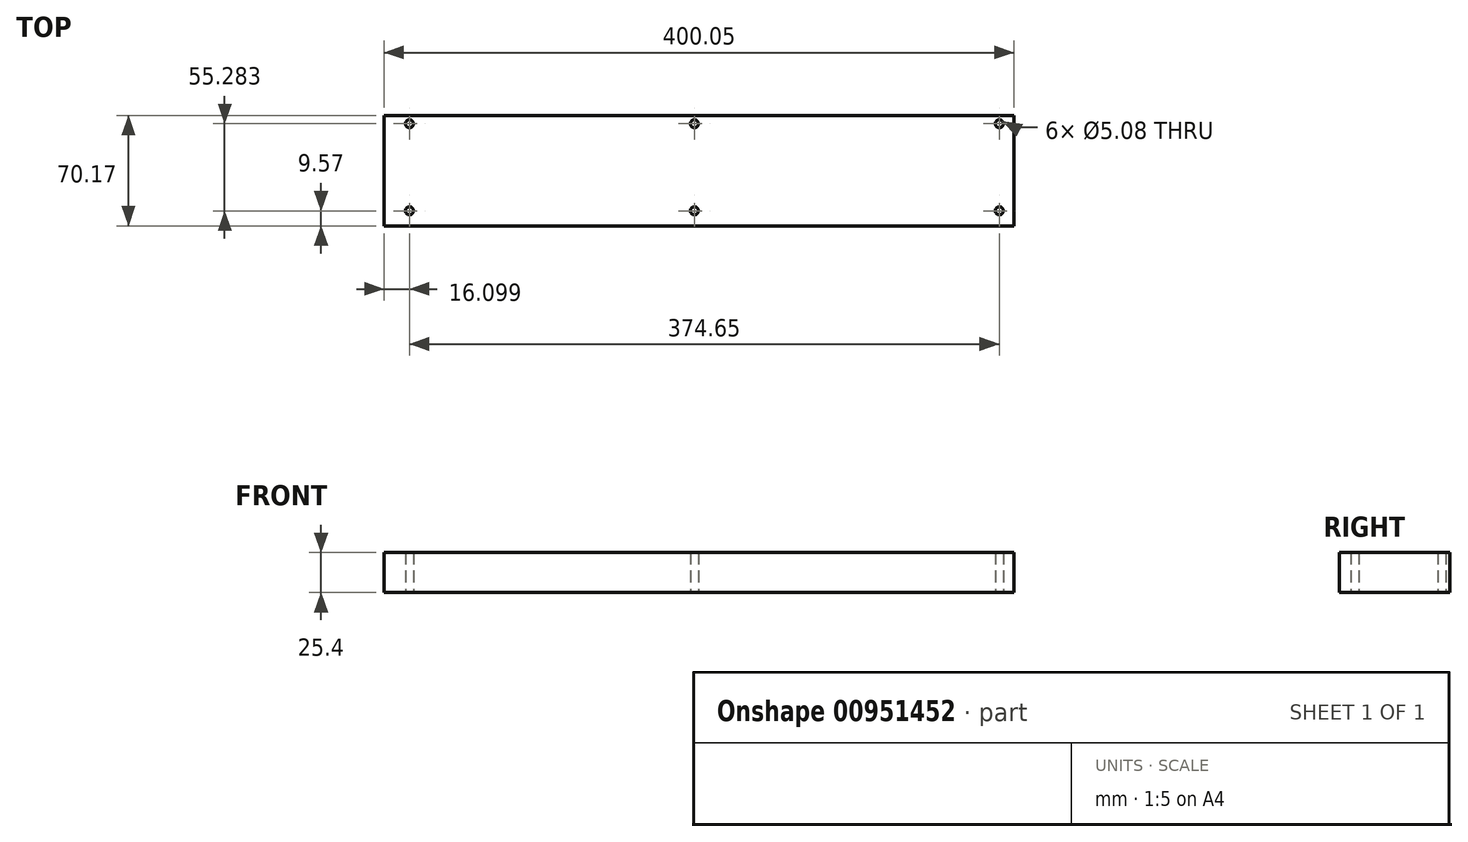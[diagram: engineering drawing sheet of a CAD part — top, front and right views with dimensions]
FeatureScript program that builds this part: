
annotation { "Feature Type Name" : "Feature", "Feature Type Description" : "" }
export const myFeature = defineFeature(function(context is Context, id is Id, definition is map)
    precondition{}
    {
        {
            var Q0;
            Q0=qCreatedBy(makeId("Top.planeOp"),FACE);
            var sketch = newSketch(context, id + "F0", { "sketchPlane" : qUnion([Q0])});
            skLineSegment(sketch, "E0.bottom", {"start": v(-398.36, 31.1) * mm, "end": v(1.69, 31.1) * mm});
            skLineSegment(sketch, "E0.top", {"start": v(-398.36, -39.06) * mm, "end": v(1.69, -39.06) * mm});
            skLineSegment(sketch, "E0.left", {"start": v(-398.36, 31.1) * mm, "end": v(-398.36, -39.06) * mm});
            skLineSegment(sketch, "E0.right", {"start": v(1.69, 31.1) * mm, "end": v(1.69, -39.06) * mm});
            skCircle(sketch, "E1", {"center": v(-7.61, -29.5) * mm, "radius": 2.54 * mm});
            skCircle(sketch, "E2", {"center": v(-201.29, -29.5) * mm, "radius": 2.54 * mm});
            skCircle(sketch, "E3", {"center": v(-382.26, -29.5) * mm, "radius": 2.54 * mm});
            skCircle(sketch, "E4", {"center": v(-382.26, 25.8) * mm, "radius": 2.54 * mm});
            skCircle(sketch, "E5", {"center": v(-201.29, 25.8) * mm, "radius": 2.54 * mm});
            skCircle(sketch, "E6", {"center": v(-7.61, 25.8) * mm, "radius": 2.54 * mm});
            skPoint(sketch, "E7", {"position": v(-33.11, 0) * mm});
            skLineSegment(sketch, "E8", {"start": v(-14.48, 19.92) * mm, "end": v(-9.4, 19.97) * mm});
            skLineSegment(sketch, "E9", {"start": v(-14.48, 19.92) * mm, "end": v(-14.82, -23.83) * mm});
            skLineSegment(sketch, "E10", {"start": v(-14.82, -23.83) * mm, "end": v(-9.74, -23.78) * mm});
            skLineSegment(sketch, "E11", {"start": v(-22.1, 19.92) * mm, "end": v(-22.44, -23.97) * mm});
            skLineSegment(sketch, "E12", {"start": v(-22.1, 19.92) * mm, "end": v(-17.02, 19.88) * mm});
            skLineSegment(sketch, "E13", {"start": v(-22.44, -23.97) * mm, "end": v(-17.36, -24) * mm});
            skPoint(sketch, "E14", {"position": v(-380.47, -23.66) * mm});
            skPoint(sketch, "E15", {"position": v(-380.47, 19.97) * mm});
            skLineSegment(sketch, "E16", {"start": v(-380.47, 19.97) * mm, "end": v(-375.39, 19.97) * mm});
            skLineSegment(sketch, "E17", {"start": v(-380.47, -23.66) * mm, "end": v(-375.39, -23.66) * mm});
            skLineSegment(sketch, "E18", {"start": v(-375.39, 19.97) * mm, "end": v(-375.39, -23.66) * mm});
            skLineSegment(sketch, "E19", {"start": v(-372.85, 19.97) * mm, "end": v(-367.77, 19.97) * mm});
            skLineSegment(sketch, "E20", {"start": v(-367.77, 19.97) * mm, "end": v(-367.77, -23.66) * mm});
            skLineSegment(sketch, "E21", {"start": v(-367.77, -23.66) * mm, "end": v(-372.85, -23.66) * mm});
            skSolve(sketch);
        }
        {
            var Q0;
            Q0 = qSketchRegion(id + "F0", true);
            extrude(context, id + "F1", {"entities" : qUnion([Q0]), "depth" : 25.4 * mm, "offsetDistance" : 25.4 * mm});
        }
    });
